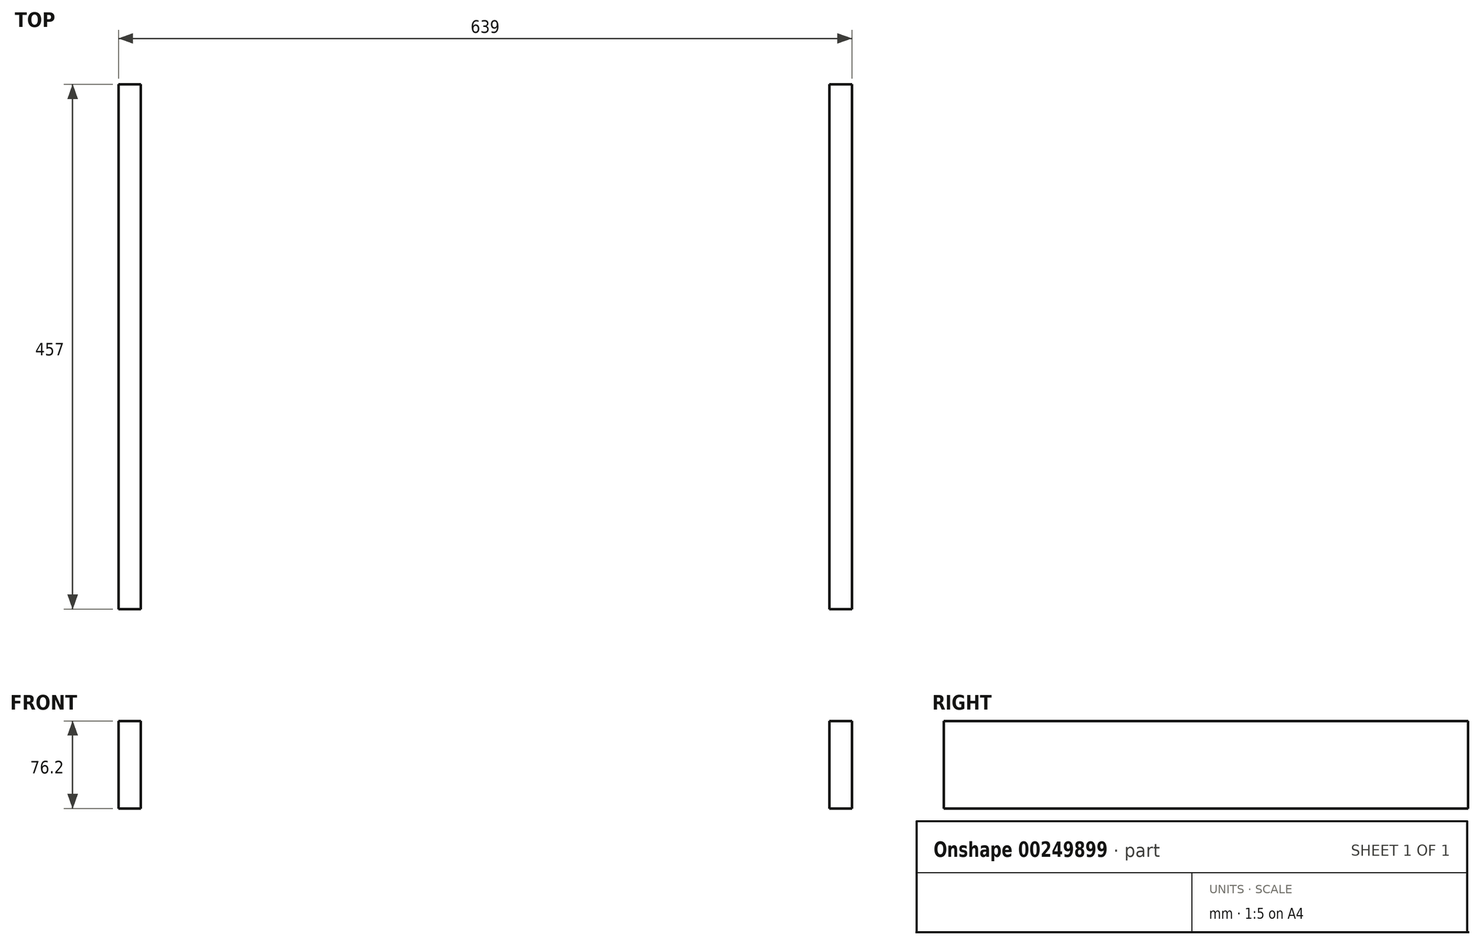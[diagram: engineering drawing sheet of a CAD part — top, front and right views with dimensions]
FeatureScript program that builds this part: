
annotation { "Feature Type Name" : "Feature", "Feature Type Description" : "" }
export const myFeature = defineFeature(function(context is Context, id is Id, definition is map)
    precondition{}
    {
        {
            var Q0;
            Q0=qCreatedBy(makeId("Front.planeOp"),FACE);
            var sketch = newSketch(context, id + "F0", { "sketchPlane" : qUnion([Q0])});
            skLineSegment(sketch, "E0.bottom", {"start": v(300, 0) * mm, "end": v(319.5, 0) * mm});
            skLineSegment(sketch, "E0.top", {"start": v(300, -76.2) * mm, "end": v(319.5, -76.2) * mm});
            skLineSegment(sketch, "E0.left", {"start": v(300, 0) * mm, "end": v(300, -76.2) * mm});
            skLineSegment(sketch, "E0.right", {"start": v(319.5, 0) * mm, "end": v(319.5, -76.2) * mm});
            skLineSegment(sketch, "E1.MirrorCS", {"start": v(-300, 0) * mm, "end": v(-319.5, 0) * mm});
            skLineSegment(sketch, "E2.MirrorCS", {"start": v(-300, -76.2) * mm, "end": v(-319.5, -76.2) * mm});
            skLineSegment(sketch, "E3.MirrorCS", {"start": v(-319.5, 0) * mm, "end": v(-319.5, -76.2) * mm});
            skLineSegment(sketch, "E4.MirrorCS", {"start": v(-300, 0) * mm, "end": v(-300, -76.2) * mm});
            skSolve(sketch);
        }
        {
            var Q0;
            Q0=makeQuery(id+"F0.imprint","IMPRINT",FACE,{"disambiguationData":[TD([[makeQuery(id+"F0.imprint","IMPRINT",EDGE,{"derivedFrom":sQuery(id+"F0.wireOp",EDGE,"E0.bottom")}),-1.0]])]});
            var Q1;
            Q1=makeQuery(id+"F0.imprint","IMPRINT",FACE,{"disambiguationData":[TD([[makeQuery(id+"F0.imprint","IMPRINT",EDGE,{"derivedFrom":sQuery(id+"F0.wireOp",EDGE,"E1.MirrorCS")}),1.0]])]});
            extrude(context, id + "F1", {"entities" : qUnion([Q0, Q1]), "oppositeDirection" : true, "depth" : 457 * mm});
        }
    });
